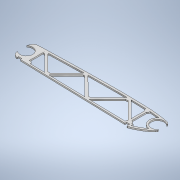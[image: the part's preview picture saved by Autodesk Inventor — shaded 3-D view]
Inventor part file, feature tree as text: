
AUTODESK INVENTOR PART (.ipt)
format: ipt  version: 2022 (Build 260153000, 153)  size: 381,440 bytes
history: native  units: mm
features: extrude x1, sketch x1
ambient origin geometry x8: Origin, YZ Plane, XZ Plane, XY Plane, X Axis, Y Axis, Z Axis, Center Point
bodies: Body1 (feature_tree)
feature tree (2):
  extrude  "Extrusion5"  Depth=10.0mm
  sketch  "Sketch1"  dims[d31=34.456mm d50=368.759386mm d57=16.0mm d69=8.0mm d70=23.0mm d71=8.0mm d73=16.0mm d80=19.0mm d81=16.0mm d82=1.0mm d83=1.0mm d84=1.0mm d85=1.0mm d86=1.0mm d87=0.8mm d88=1.0mm d90=19.0mm d94=5.0mm d95=5.0mm d105=5.0mm d106=5.0mm d108=2.0mm d109=19.0mm d114=5.0mm d115=5.0mm d116=24.0mm d117=2.5mm d118=2.5mm d123=2.5mm d124=2.5mm d125=10.0mm d126=24.0mm d127=24.0mm d128=27.0mm d135=0.5mm d136=45.0deg d139=7.0mm d165=45.0deg d169=27.0mm d175=90.0deg d181=45.0deg d185=7.0mm d186=45.0deg d190=7.0mm d191=45.0deg d197=90.0deg d203=90.0deg d206=7.0mm d207=2.0mm d208=0.0mm]
